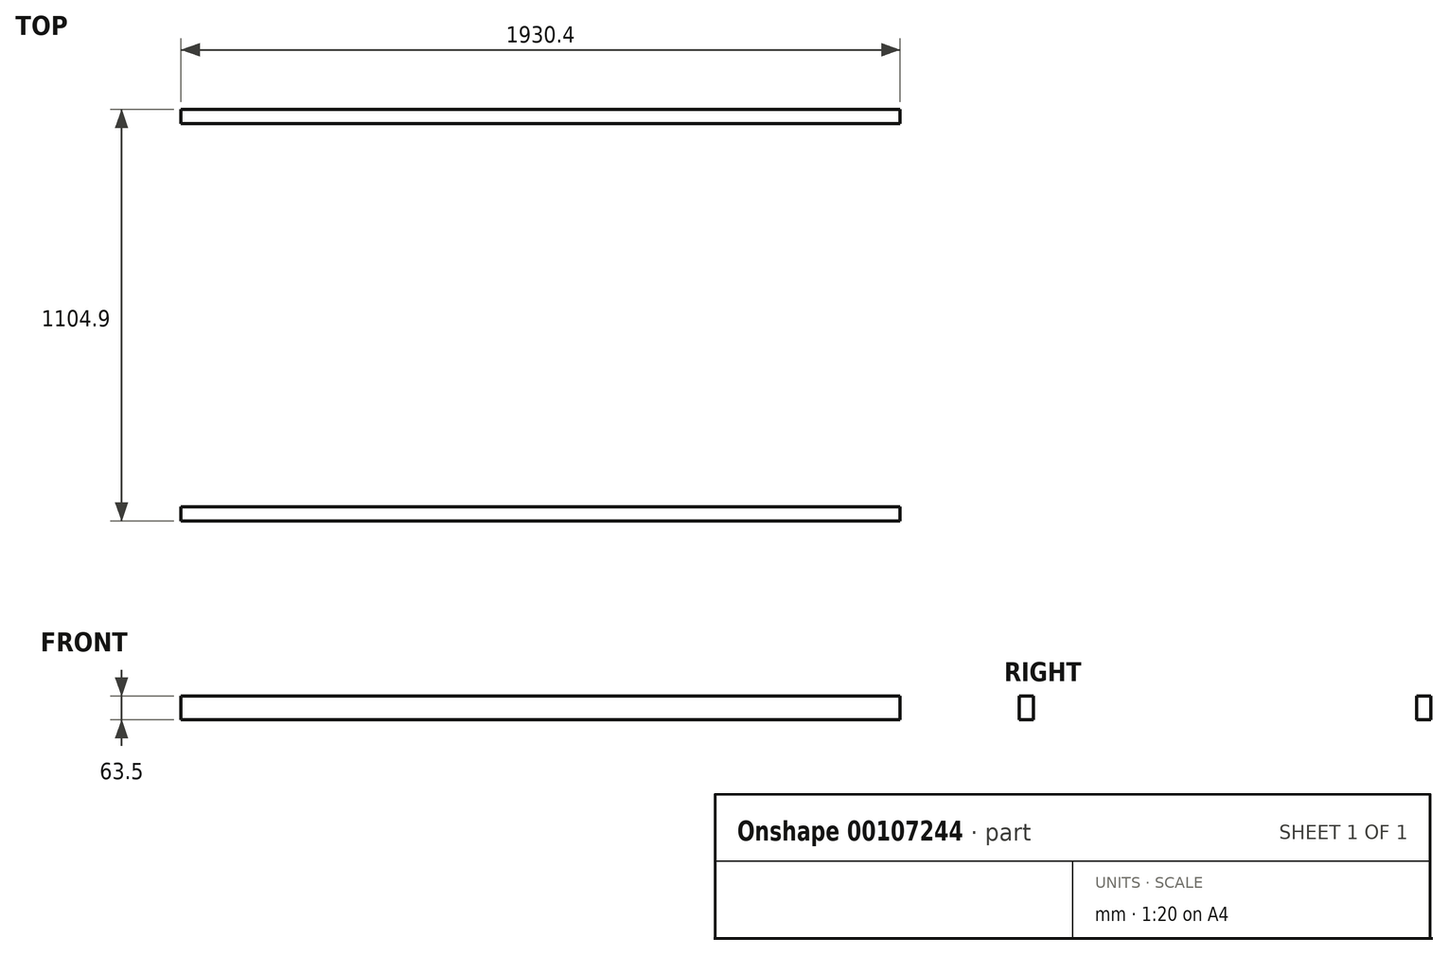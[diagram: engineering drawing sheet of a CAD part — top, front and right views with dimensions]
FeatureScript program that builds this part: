
annotation { "Feature Type Name" : "Feature", "Feature Type Description" : "" }
export const myFeature = defineFeature(function(context is Context, id is Id, definition is map)
    precondition{}
    {
        {
            var Q0;
            Q0=qCreatedBy(makeId("Front.planeOp"),FACE);
            var sketch = newSketch(context, id + "F0", { "sketchPlane" : qUnion([Q0])});
            skLineSegment(sketch, "E0.bottom", {"start": v(-967.46, -18.12) * mm, "end": v(962.94, -18.12) * mm});
            skLineSegment(sketch, "E0.top", {"start": v(-967.46, -81.62) * mm, "end": v(962.94, -81.62) * mm});
            skLineSegment(sketch, "E0.left", {"start": v(-967.46, -18.12) * mm, "end": v(-967.46, -81.62) * mm});
            skLineSegment(sketch, "E0.right", {"start": v(962.94, -18.12) * mm, "end": v(962.94, -81.62) * mm});
            skSolve(sketch);
        }
        {
            var Q0;
            Q0=makeQuery(id+"F0.imprint","IMPRINT",FACE,{"disambiguationData":[TD([[makeQuery(id+"F0.imprint","IMPRINT",EDGE,{"derivedFrom":sQuery(id+"F0.wireOp",EDGE,"E0.bottom")}),-1.0]])]});
            extrude(context, id + "F1", {"entities" : qUnion([Q0]), "depth" : 38.1 * mm});
        }
        {
            var Q0;
            Q0=makeQuery(id+"F1.opExtrude","SWEPT_BODY",BODY,{"disambiguationData":[OSD([sQuery(id+"F0.wireOp",EDGE,"E0.bottom"),sQuery(id+"F0.wireOp",EDGE,"E0.top"),sQuery(id+"F0.wireOp",EDGE,"E0.left"),sQuery(id+"F0.wireOp",EDGE,"E0.right")])]});
            transform(context, id + "F2", {"entities" : qUnion([Q0]), "transformType" : TransformType.TRANSLATION_3D, "dx" : 0 * mm, "dy" : 1066.8 * mm, "dz" : 0 * mm, "makeCopy" : true});
        }
    });
